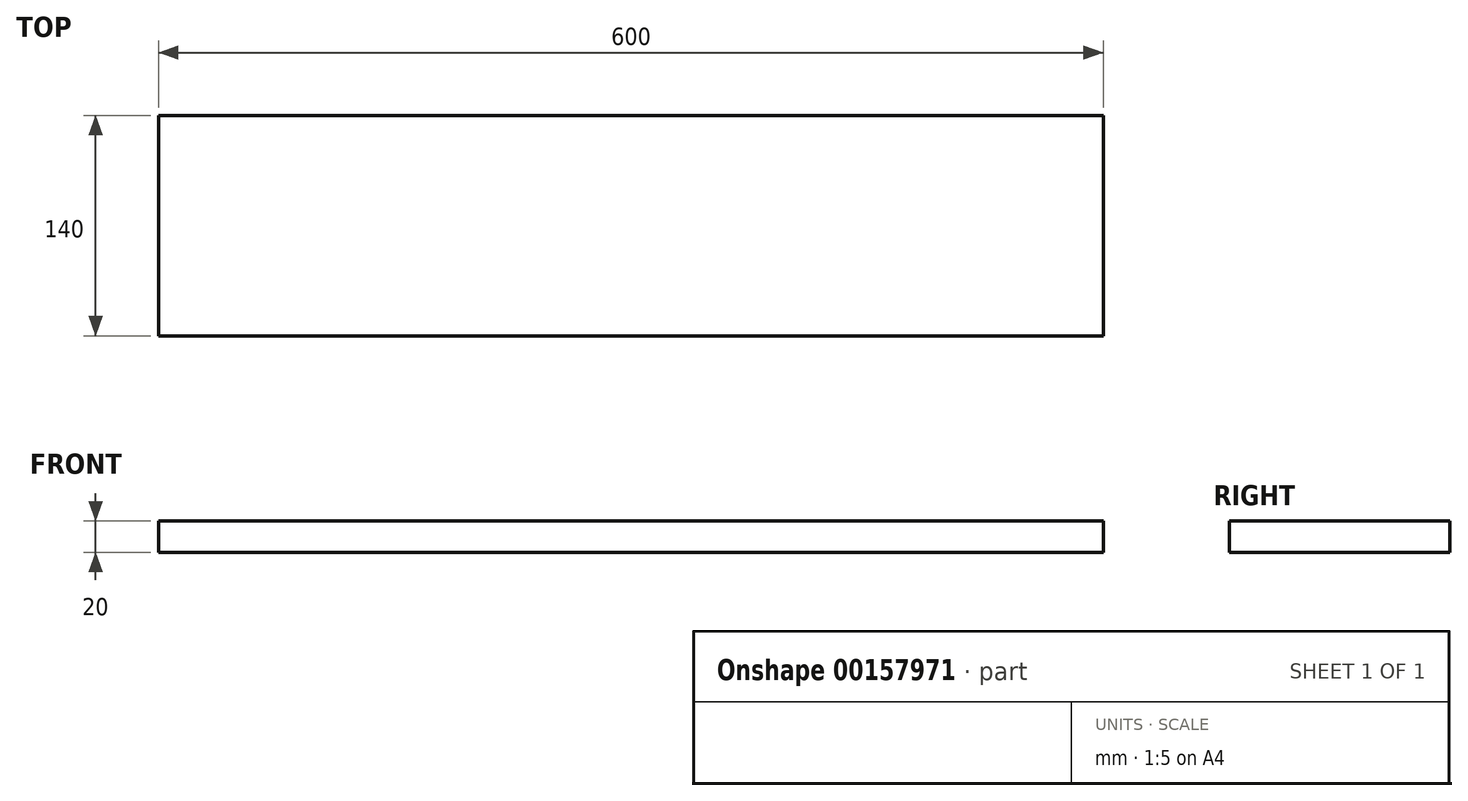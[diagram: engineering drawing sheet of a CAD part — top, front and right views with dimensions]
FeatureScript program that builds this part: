
annotation { "Feature Type Name" : "Feature", "Feature Type Description" : "" }
export const myFeature = defineFeature(function(context is Context, id is Id, definition is map)
    precondition{}
    {
        {
            var Q0;
            Q0=qCreatedBy(makeId("Top.planeOp"),FACE);
            var sketch = newSketch(context, id + "F0", { "sketchPlane" : qUnion([Q0])});
            skLineSegment(sketch, "E0.bottom", {"start": v(-300, 70) * mm, "end": v(300, 70) * mm});
            skLineSegment(sketch, "E0.top", {"start": v(-300, -70) * mm, "end": v(300, -70) * mm});
            skLineSegment(sketch, "E0.left", {"start": v(-300, 70) * mm, "end": v(-300, -70) * mm});
            skLineSegment(sketch, "E0.right", {"start": v(300, 70) * mm, "end": v(300, -70) * mm});
            skPoint(sketch, "E0.middle", {"position": v(0, 0) * mm});
            skSolve(sketch);
        }
        {
            var Q0;
            Q0=makeQuery(id+"F0.imprint","IMPRINT",FACE,{"disambiguationData":[TD([[makeQuery(id+"F0.imprint","IMPRINT",EDGE,{"derivedFrom":sQuery(id+"F0.wireOp",EDGE,"E0.bottom")}),-1.0]])]});
            extrude(context, id + "F1", {"entities" : qUnion([Q0]), "endBound" : BoundingType.SYMMETRIC, "depth" : 20 * mm});
        }
    });
